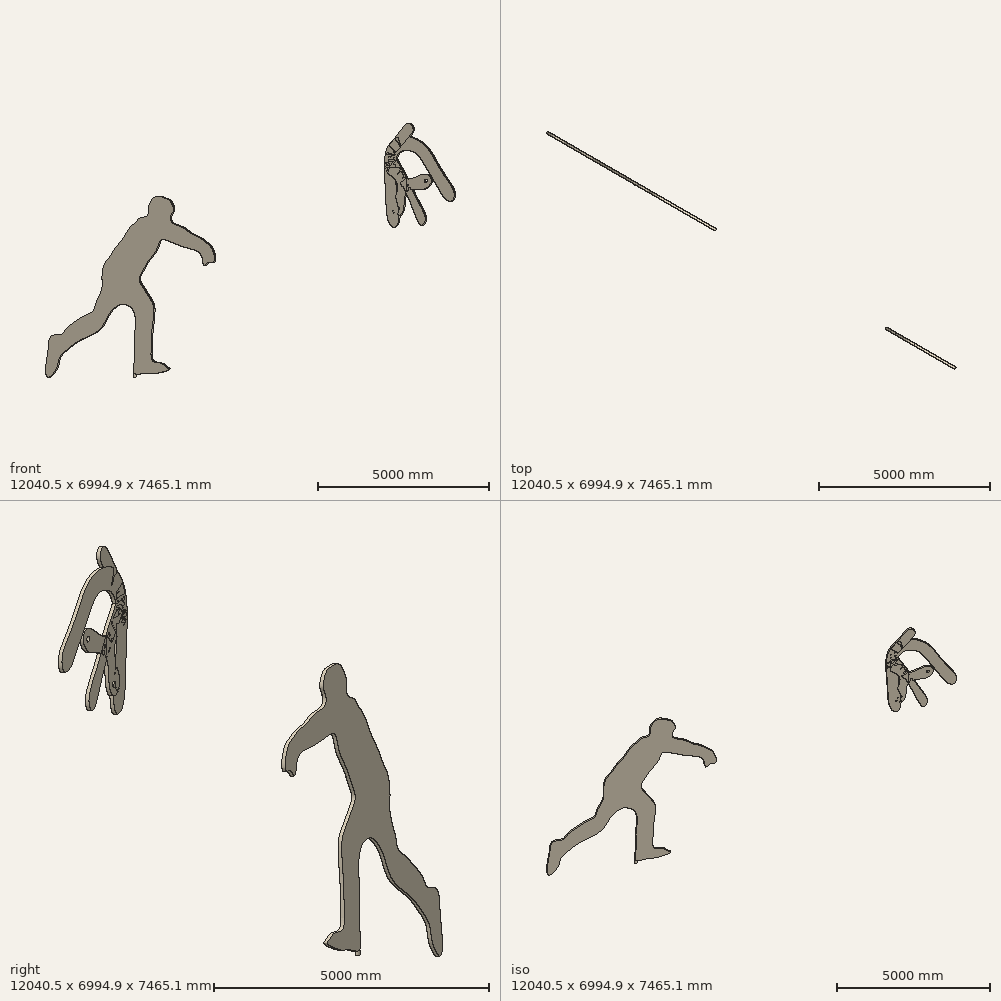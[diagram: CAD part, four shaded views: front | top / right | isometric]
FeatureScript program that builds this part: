
annotation { "Feature Type Name" : "Feature", "Feature Type Description" : "" }
export const myFeature = defineFeature(function(context is Context, id is Id, definition is map)
    precondition{}
    {
        {
            var Q0;
            Q0=qCreatedBy(makeId("Front.planeOp"),FACE);
            var sketch = newSketch(context, id + "F0", { "sketchPlane" : qUnion([Q0])});
            skFitSpline(sketch, "E0", {"points": [v(0, 0) * mm, v(93.84, 0) * mm, v(220.46, 0) * mm, v(285.76, 9.7) * mm, v(348.27, 22.1) * mm, v(391.42, 43.15) * mm, v(359.09, 67.27) * mm, v(316.58, 97.78) * mm, v(237.34, 113.23) * mm, v(197.59, 136.33) * mm, v(188.64, 263.09) * mm, v(199.94, 440.02) * mm, v(209.82, 503.11) * mm, v(217.6, 584.55) * mm, v(213.18, 672.15) * mm, v(170.26, 745.69) * mm, v(102.9, 839.71) * mm, v(55.93, 913.27) * mm, v(65.3, 959.85) * mm, v(107, 1025.26) * mm, v(152.74, 1092.73) * mm, v(234.68, 1184.87) * mm, v(274.15, 1264.51) * mm, v(308.58, 1311.22) * mm, v(397.72, 1293.84) * mm, v(527.7, 1248.53) * mm, v(665.59, 1213.4) * mm, v(718.41, 1193.67) * mm, v(757.43, 1153.59) * mm, v(770.43, 1099.12) * mm, v(792.7, 1055.94) * mm, v(841.27, 1089.23) * mm, v(875.69, 1083.9) * mm, v(903.6, 1106.4) * mm, v(873.36, 1228.85) * mm, v(829.87, 1271.33) * mm, v(737.42, 1332.85) * mm, v(643.37, 1372.93) * mm, v(541.2, 1434.38) * mm, v(433.53, 1474.33) * mm, v(408.42, 1512.78) * mm, v(418.02, 1553.5) * mm, v(439.05, 1585.48) * mm, v(440.3, 1621.87) * mm, v(403.29, 1690.15) * mm, v(355.25, 1716.26) * mm, v(295.74, 1735.07) * mm, v(256.57, 1737.18) * mm, v(207.87, 1710.23) * mm, v(170.26, 1658.7) * mm, v(158.24, 1625.76) * mm, v(162.28, 1585.73) * mm, v(147.76, 1547.3) * mm, v(111.8, 1532.71) * mm, v(61.33, 1522.46) * mm, v(18.48, 1481.69) * mm, v(-31.66, 1445.27) * mm, v(-90.07, 1376.85) * mm, v(-136.95, 1311.36) * mm, v(-235.33, 1202.17) * mm, v(-270.8, 1148.33) * mm, v(-326.4, 1087.18) * mm, v(-360.07, 1005.71) * mm, v(-366.22, 919.92) * mm, v(-365.3, 847.23) * mm, v(-404.13, 749.46) * mm, v(-437.9, 682) * mm, v(-465.6, 614.17) * mm, v(-542.6, 575.96) * mm, v(-634.27, 528.42) * mm, v(-775.1, 430.74) * mm, v(-813.85, 386.08) * mm, v(-915.09, 376.7) * mm, v(-963.83, 327.75) * mm, v(-970.42, 270.45) * mm, v(-989.41, 152.4) * mm, v(-1002.1, 71.41) * mm, v(-1002.12, 0) * mm, v(-977.03, -38.13) * mm, v(-916.04, 0) * mm, v(-870.9, 70.01) * mm, v(-842.5, 156.52) * mm, v(-760.12, 233) * mm, v(-663.9, 299.78) * mm, v(-550.22, 352.36) * mm, v(-449.06, 394.51) * mm, v(-362.6, 460.73) * mm, v(-302.52, 554.93) * mm, v(-245.37, 624.67) * mm, v(-164.03, 674.76) * mm, v(-115.56, 680.57) * mm, v(-38.5, 644.86) * mm, v(0, 584.52) * mm, v(15.4, 495.83) * mm, v(0, 372.89) * mm, v(0, 287.08) * mm, v(0, 134.3) * mm, v(0, 0) * mm]});
            skFitSpline(sketch, "E1", {"points": [v(3065.45, 1916.83) * mm, v(3021.98, 1976.49) * mm, v(2982.01, 2029.66) * mm, v(2912.08, 2076) * mm, v(2849.72, 2074.15) * mm, v(2829.3, 2026.66) * mm, v(2865.16, 1964.85) * mm, v(2937.57, 1904.57) * mm, v(2973.3, 1852.8) * mm, v(2974.54, 1795.55) * mm, v(2945.16, 1716.81) * mm, v(2914.43, 1649.87) * mm, v(2936.89, 1563.2) * mm, v(3005.75, 1549.29) * mm, v(3046.04, 1635.43) * mm, v(3058.75, 1736.5) * mm, v(3099.14, 1787.73) * mm, v(3175.53, 1804.52) * mm, v(3278.77, 1806.9) * mm, v(3337.25, 1842.54) * mm, v(3356.4, 1892.68) * mm, v(3312.05, 1949.02) * mm, v(3228.3, 1941.52) * mm, v(3133.32, 1908.12) * mm, v(3065.45, 1916.83) * mm]});
            skCircle(sketch, "E2", {"center": v(2890.9, 2029.33) * mm, "radius": 13.3 * mm});
            skCircle(sketch, "E3", {"center": v(2982.14, 1611.9) * mm, "radius": 19.43 * mm});
            skCircle(sketch, "E4", {"center": v(3295.66, 1886.7) * mm, "radius": 17.38 * mm});
            skSolve(sketch);
        }
        {
            var Q0;
            Q0=qSketchRegion(id+"F0",true);
            extrude(context, id + "F1", {"entities" : qUnion([Q0]), "depth" : 25 * mm, "offsetDistance" : 25 * mm, "symmetric" : true});
        }
        {
            var Q0;
            Q0=qCreatedBy(makeId("Front.planeOp"),FACE);
            var sketch = newSketch(context, id + "F2", { "sketchPlane" : qUnion([Q0])});
            skFitSpline(sketch, "E5", {"points": [v(3242.8, 1452.6) * mm, v(3128.5, 1651.93) * mm, v(2984.12, 1894.83) * mm, v(2850.48, 2150.35) * mm, v(2963.67, 2323.52) * mm, v(3104.56, 2449.87) * mm, v(3150.95, 2392.53) * mm, v(3109.5, 2320.67) * mm, v(2997.55, 2202.28) * mm, v(2950.35, 2144.94) * mm, v(2980.43, 2068.49) * mm, v(3053.27, 1957.06) * mm, v(3184.77, 1719.34) * mm, v(3287.04, 1505) * mm, v(3242.8, 1452.6) * mm]});
            skSolve(sketch);
        }
        {
            var Q0;
            Q0=qSketchRegion(id+"F2",true);
            extrude(context, id + "F3", {"entities" : qUnion([Q0]), "depth" : 25 * mm, "offsetDistance" : 25 * mm, "symmetric" : true});
        }
        {
            var Q0;
            Q0=qCreatedBy(makeId("Front.planeOp"),FACE);
            var sketch = newSketch(context, id + "F4", { "sketchPlane" : qUnion([Q0])});
            skFitSpline(sketch, "E6", {"points": [v(2879.2, 1474.49) * mm, v(2838, 1778.78) * mm, v(2823.97, 1963.82) * mm, v(2853.25, 2195.98) * mm, v(3021.32, 2325.91) * mm, v(3286.22, 2232.5) * mm, v(3430.41, 2040.35) * mm, v(3568.51, 1855.75) * mm, v(3613.78, 1768.05) * mm, v(3592.77, 1692.02) * mm, v(3516.3, 1707.91) * mm, v(3449.32, 1790.95) * mm, v(3344.2, 1940.74) * mm, v(3253.58, 2081.04) * mm, v(3155.87, 2169.4) * mm, v(3036.47, 2180.18) * mm, v(2976.32, 2136.93) * mm, v(2953.8, 2070.09) * mm, v(2951.4, 1956.46) * mm, v(2955.97, 1859.67) * mm, v(2967.16, 1712.18) * mm, v(2989.62, 1543.7) * mm, v(2952.68, 1435.27) * mm, v(2879.2, 1474.49) * mm]});
            skSolve(sketch);
        }
        {
            var Q0;
            Q0=qSketchRegion(id+"F4",true);
            extrude(context, id + "F5", {"entities" : qUnion([Q0]), "depth" : 25 * mm, "offsetDistance" : 25 * mm, "symmetric" : true});
        }
        {
            var Q0;
            Q0=makeQuery(id+"F1.opExtrude","SWEPT_BODY",BODY,{"disambiguationData":[OSD([sQuery(id+"F0.wireOp",EDGE,"E1"),sQuery(id+"F0.wireOp",EDGE,"E2"),sQuery(id+"F0.wireOp",EDGE,"E3"),sQuery(id+"F0.wireOp",EDGE,"E4")])]});
            var Q1;
            Q1=makeQuery(id+"F1.opExtrude","SWEPT_BODY",BODY,{"disambiguationData":[OSD([sQuery(id+"F0.wireOp",EDGE,"E0")])]});
            var Q2;
            Q2=makeQuery(id+"F5.opExtrude","SWEPT_BODY",BODY,{"disambiguationData":[OSD([sQuery(id+"F4.wireOp",EDGE,"E6")])]});
            var Q3;
            Q3=makeQuery(id+"F3.opExtrude","SWEPT_BODY",BODY,{"disambiguationData":[OSD([sQuery(id+"F2.wireOp",EDGE,"E5")])]});
            var Q4;
            Q4=qCreatedBy(makeId("Origin.pointOp"),VERTEX);
            transform(context, id + "F6", {"entities" : qUnion([Q0, Q1, Q2, Q3]), "transformType" : TransformType.SCALE_UNIFORMLY, "scale" : 3, "scalePoint" : qUnion([Q4]), "makeCopy" : false});
        }
        {
            var Q0;
            Q0=qCreatedBy(makeId("Top.planeOp"),FACE);
            var sketch = newSketch(context, id + "F7", { "sketchPlane" : qUnion([Q0])});
            skCircle(sketch, "E7", {"center": v(0, 0) * mm, "radius": 50 * mm});
            skSolve(sketch);
        }
        {
            var Q0;
            Q0 = qSketchRegion(id + "F7", true);
            extrude(context, id + "F8", {"entities" : qUnion([Q0]), "oppositeDirection" : true, "depth" : 100 * mm, "offsetDistance" : 25 * mm});
        }
        {
            var Q0;
            Q0=makeQuery(id+"F1.opExtrude","SWEPT_BODY",BODY,{"disambiguationData":[OSD([sQuery(id+"F0.wireOp",EDGE,"E0")])]});
            var Q1;
            Q1=makeQuery(id+"F1.opExtrude","SWEPT_BODY",BODY,{"disambiguationData":[OSD([sQuery(id+"F0.wireOp",EDGE,"E1"),sQuery(id+"F0.wireOp",EDGE,"E2"),sQuery(id+"F0.wireOp",EDGE,"E3"),sQuery(id+"F0.wireOp",EDGE,"E4")])]});
            var Q2;
            Q2=makeQuery(id+"F3.opExtrude","SWEPT_BODY",BODY,{"disambiguationData":[OSD([sQuery(id+"F2.wireOp",EDGE,"E5")])]});
            var Q3;
            Q3=makeQuery(id+"F5.opExtrude","SWEPT_BODY",BODY,{"disambiguationData":[OSD([sQuery(id+"F4.wireOp",EDGE,"E6")])]});
            var Q4;
            Q4=makeQuery(id+"F8.opExtrude","SWEPT_FACE",FACE,{"disambiguationData":[OSD([sQuery(id+"F7.wireOp",EDGE,"E7")])]});
            transform(context, id + "F9", {"entities" : qUnion([Q0, Q1, Q2, Q3]), "transformType" : TransformType.ROTATION, "transformAxis" : qUnion([Q4]), "angle" : 30 * degree, "oppositeDirection" : true, "makeCopy" : false});
        }
    });
